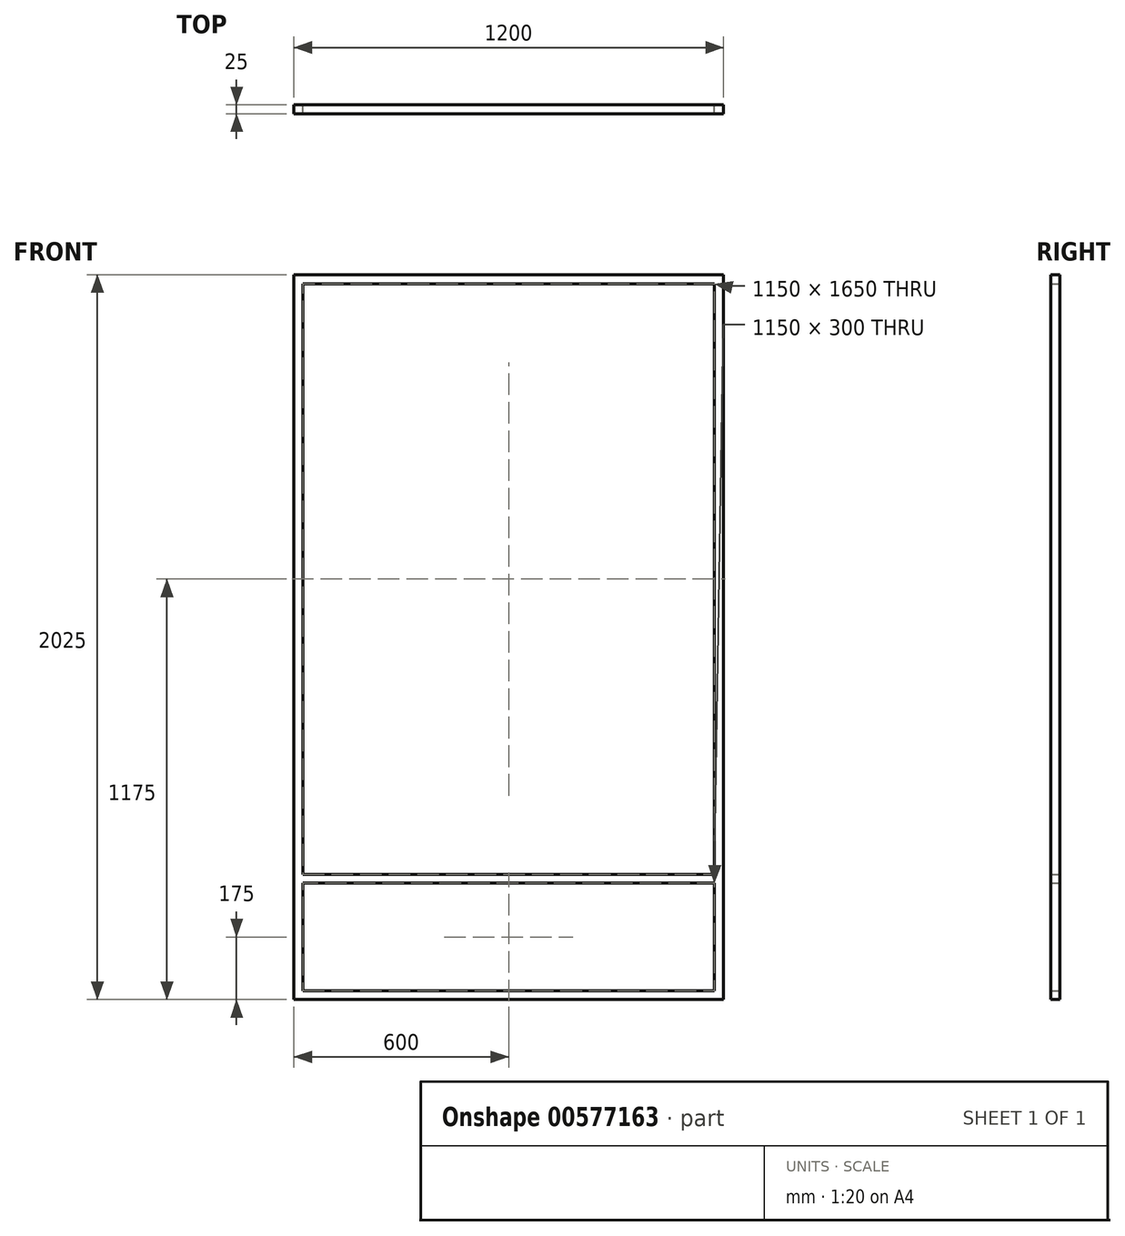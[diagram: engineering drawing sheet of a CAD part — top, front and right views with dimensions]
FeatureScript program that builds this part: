
annotation { "Feature Type Name" : "Feature", "Feature Type Description" : "" }
export const myFeature = defineFeature(function(context is Context, id is Id, definition is map)
    precondition{}
    {
        {
            var Q0;
            Q0=qCreatedBy(makeId("Front.planeOp"),FACE);
            var sketch = newSketch(context, id + "F0", { "sketchPlane" : qUnion([Q0])});
            skLineSegment(sketch, "E0.bottom", {"start": v(0, 0) * mm, "end": v(1200, 0) * mm});
            skLineSegment(sketch, "E0.top", {"start": v(0, 2025) * mm, "end": v(1200, 2025) * mm});
            skLineSegment(sketch, "E0.left", {"start": v(0, 0) * mm, "end": v(0, 2025) * mm});
            skLineSegment(sketch, "E0.right", {"start": v(1200, 0) * mm, "end": v(1200, 2025) * mm});
            skLineSegment(sketch, "E1.0", {"start": v(25, 25) * mm, "end": v(25, 2000) * mm});
            skLineSegment(sketch, "E1.1", {"start": v(25, 25) * mm, "end": v(1175, 25) * mm});
            skLineSegment(sketch, "E1.2", {"start": v(1175, 25) * mm, "end": v(1175, 2000) * mm});
            skLineSegment(sketch, "E1.3", {"start": v(25, 2000) * mm, "end": v(1175, 2000) * mm});
            skLineSegment(sketch, "E2", {"start": v(25, 325) * mm, "end": v(1175, 325) * mm});
            skLineSegment(sketch, "E3", {"start": v(25, 350) * mm, "end": v(1175, 350) * mm});
            skSolve(sketch);
        }
        {
            var Q0;
            Q0=makeQuery(id+"F0.imprint","IMPRINT",FACE,{"disambiguationData":[TD([[makeQuery(id+"F0.imprint","IMPRINT",EDGE,{"derivedFrom":sQuery(id+"F0.wireOp",EDGE,"E0.bottom")}),1.0]])]});
            var Q1;
            {var subQ0=sQuery(id+"F0.wireOp",EDGE,"E2");Q1=makeQuery(id+"F0.imprint","IMPRINT",FACE,{"disambiguationData":[TD([[makeQuery(id+"F0.imprint","IMPRINT",EDGE,{"derivedFrom":subQ0}),1.0]])]});}
            extrude(context, id + "F1", {"entities" : qUnion([Q0, Q1]), "depth" : 25 * mm, "offsetDistance" : 25 * mm});
        }
    });
